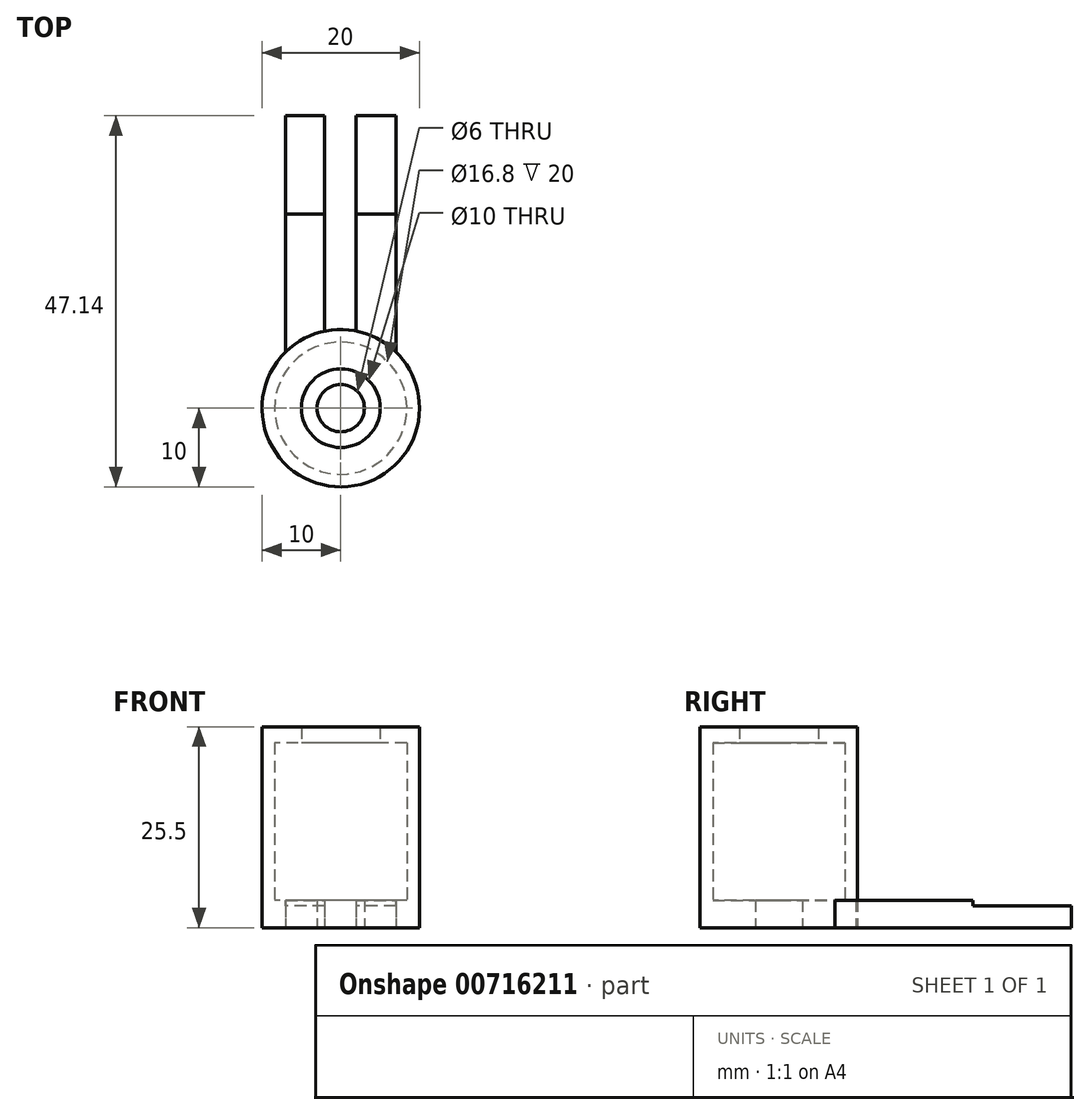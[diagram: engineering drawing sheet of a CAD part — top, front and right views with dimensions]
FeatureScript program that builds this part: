
annotation { "Feature Type Name" : "Feature", "Feature Type Description" : "" }
export const myFeature = defineFeature(function(context is Context, id is Id, definition is map)
    precondition{}
    {
        {
            var Q0;
            Q0=qCreatedBy(makeId("Top.planeOp"),FACE);
            var sketch = newSketch(context, id + "F0", { "sketchPlane" : qUnion([Q0])});
            skCircle(sketch, "E0", {"center": v(0, 0) * mm, "radius": 3 * mm});
            skArc(sketch, "E1.0", {"start": v(-7, 7.14) * mm, "mid": v(0, -10) * mm, "end": v(7, 7.14) * mm});
            skLineSegment(sketch, "E2.top", {"start": v(7, 37.14) * mm, "end": v(1.94, 37.14) * mm});
            skLineSegment(sketch, "E2.left", {"start": v(7, 7.14) * mm, "end": v(7, 37.14) * mm});
            skLineSegment(sketch, "E2.right", {"start": v(-7, 7.14) * mm, "end": v(-7, 37.14) * mm});
            skPoint(sketch, "E2.middle", {"position": v(0, 22.14) * mm});
            skLineSegment(sketch, "E3.left", {"start": v(1.94, 37.14) * mm, "end": v(1.94, 9.81) * mm});
            skLineSegment(sketch, "E3.right", {"start": v(-2.06, 37.14) * mm, "end": v(-2.06, 9.78) * mm});
            skLineSegment(sketch, "E4.trimOffspring", {"start": v(-2.06, 37.14) * mm, "end": v(-7, 37.14) * mm});
            skArc(sketch, "E5", {"start": v(1.94, 9.81) * mm, "mid": v(-0.07, 10) * mm, "end": v(-2.06, 9.78) * mm});
            skSolve(sketch);
        }
        {
            var Q0;
            Q0 = qSketchRegion(id + "F0", true);
            extrude(context, id + "F1", {"entities" : qUnion([Q0]), "depth" : 3.5 * mm, "offsetDistance" : 25 * mm});
        }
        {
            var Q0;
            Q0=makeQuery(id+"F1.opExtrude","CAP_FACE",FACE,{"disambiguationData":[OSD([sQuery(id+"F0.wireOp",EDGE,"E0"),sQuery(id+"F0.wireOp",EDGE,"E1.0"),sQuery(id+"F0.wireOp",EDGE,"E2.top"),sQuery(id+"F0.wireOp",EDGE,"E2.left"),sQuery(id+"F0.wireOp",EDGE,"E2.right"),sQuery(id+"F0.wireOp",EDGE,"E3.left"),sQuery(id+"F0.wireOp",EDGE,"E3.right"),sQuery(id+"F0.wireOp",EDGE,"E4.trimOffspring"),sQuery(id+"F0.wireOp",EDGE,"E5")])],"isStart":false});
            var sketch = newSketch(context, id + "F2", { "sketchPlane" : qUnion([Q0])});
            skLineSegment(sketch, "E6.bottom", {"start": v(-7, 37.14) * mm, "end": v(7, 37.14) * mm});
            skLineSegment(sketch, "E6.top", {"start": v(-7, 24.64) * mm, "end": v(7, 24.64) * mm});
            skLineSegment(sketch, "E6.left", {"start": v(-7, 37.14) * mm, "end": v(-7, 24.64) * mm});
            skLineSegment(sketch, "E6.right", {"start": v(7, 37.14) * mm, "end": v(7, 24.64) * mm});
            skSolve(sketch);
        }
        {
            var Q0;
            Q0 = qSketchRegion(id + "F2", true);
            extrude(context, id + "F3", {"entities" : qUnion([Q0]), "operationType" : NewBodyOperationType.REMOVE, "oppositeDirection" : true, "depth" : .7 * mm, "offsetDistance" : 25 * mm});
        }
        {
            var Q0;
            Q0=makeQuery(id+"F1.opExtrude","CAP_FACE",FACE,{"disambiguationData":[OSD([sQuery(id+"F0.wireOp",EDGE,"E0"),sQuery(id+"F0.wireOp",EDGE,"E1.0"),sQuery(id+"F0.wireOp",EDGE,"E2.top"),sQuery(id+"F0.wireOp",EDGE,"E2.left"),sQuery(id+"F0.wireOp",EDGE,"E2.right"),sQuery(id+"F0.wireOp",EDGE,"E3.left"),sQuery(id+"F0.wireOp",EDGE,"E3.right"),sQuery(id+"F0.wireOp",EDGE,"E4.trimOffspring"),sQuery(id+"F0.wireOp",EDGE,"E5")])],"isStart":false});
            var sketch = newSketch(context, id + "F4", { "sketchPlane" : qUnion([Q0])});
            skCircle(sketch, "E7", {"center": v(0, 0) * mm, "radius": 10 * mm});
            skCircle(sketch, "E8.0", {"center": v(0, 0) * mm, "radius": 8.4 * mm});
            skSolve(sketch);
        }
        {
            var Q0;
            Q0 = qSketchRegion(id + "F4", true);
            extrude(context, id + "F5", {"entities" : qUnion([Q0]), "operationType" : NewBodyOperationType.ADD, "depth" : 20 * mm, "offsetDistance" : 25 * mm});
        }
        {
            var Q0;
            Q0=makeQuery(id+"F5.opExtrude","CAP_FACE",FACE,{"disambiguationData":[OSD([sQuery(id+"F4.wireOp",EDGE,"E7"),sQuery(id+"F4.wireOp",EDGE,"E8.0")])],"isStart":false});
            var sketch = newSketch(context, id + "F6", { "sketchPlane" : qUnion([Q0])});
            skCircle(sketch, "E9.0", {"center": v(0, 0) * mm, "radius": 10 * mm});
            skCircle(sketch, "E10", {"center": v(0, 0) * mm, "radius": 5 * mm});
            skSolve(sketch);
        }
        {
            var Q0;
            Q0 = qSketchRegion(id + "F6", true);
            extrude(context, id + "F7", {"entities" : qUnion([Q0]), "operationType" : NewBodyOperationType.ADD, "depth" : 2 * mm, "offsetDistance" : 25 * mm});
        }
    });
